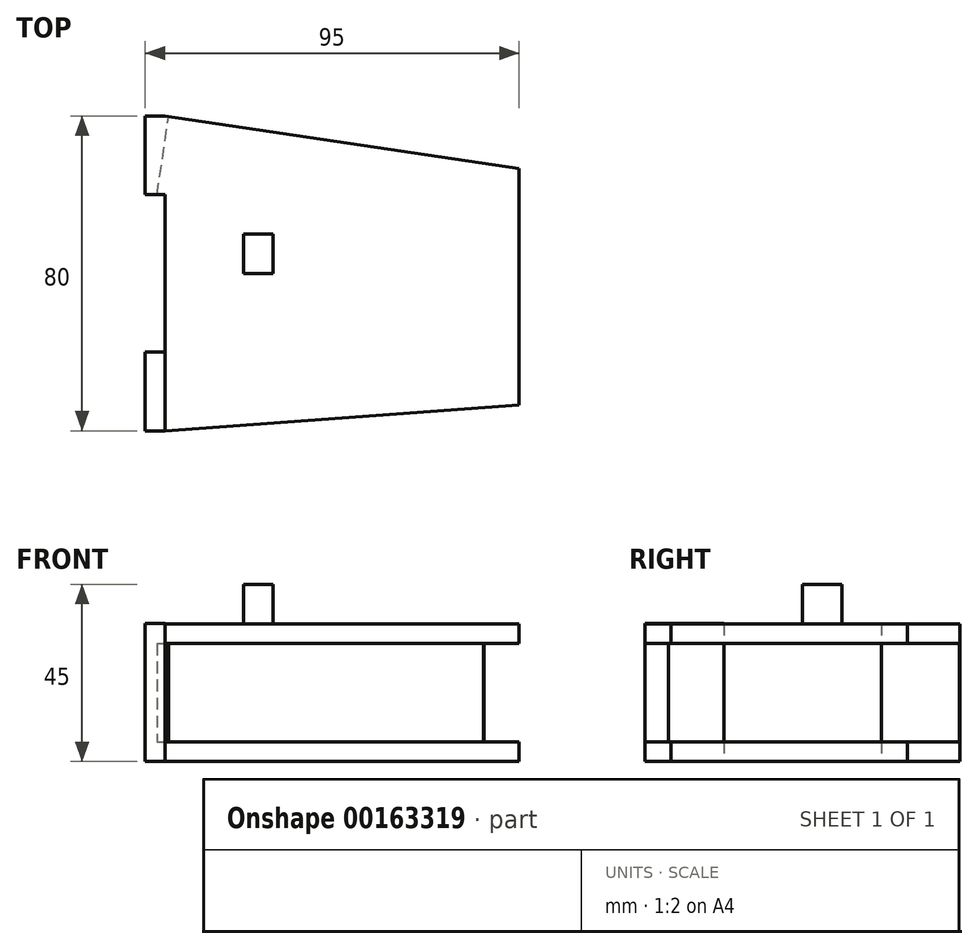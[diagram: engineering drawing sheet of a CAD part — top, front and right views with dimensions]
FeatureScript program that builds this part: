
annotation { "Feature Type Name" : "Feature", "Feature Type Description" : "" }
export const myFeature = defineFeature(function(context is Context, id is Id, definition is map)
    precondition{}
    {
        {
            var Q0;
            Q0=qCreatedBy(makeId("Top.planeOp"),FACE);
            var sketch = newSketch(context, id + "F0", { "sketchPlane" : qUnion([Q0])});
            skLineSegment(sketch, "E0", {"start": v(-88.53, 60) * mm, "end": v(-88.53, -20) * mm});
            skLineSegment(sketch, "E1", {"start": v(1.47, -13.38) * mm, "end": v(1.47, 46.62) * mm});
            skLineSegment(sketch, "E2", {"start": v(1.47, 46.62) * mm, "end": v(-88.53, 60) * mm});
            skLineSegment(sketch, "E3", {"start": v(-88.53, -20) * mm, "end": v(1.47, -13.38) * mm});
            skLineSegment(sketch, "E4", {"start": v(-88.53, 40) * mm, "end": v(-88.53, 0) * mm});
            skLineSegment(sketch, "E5.bottom", {"start": v(-88.53, 60) * mm, "end": v(-93.53, 60) * mm});
            skLineSegment(sketch, "E5.top", {"start": v(-88.53, 40) * mm, "end": v(-93.53, 40) * mm});
            skLineSegment(sketch, "E5.left", {"start": v(-88.53, 60) * mm, "end": v(-88.53, 40) * mm});
            skLineSegment(sketch, "E5.right", {"start": v(-93.53, 60) * mm, "end": v(-93.53, 40) * mm});
            skLineSegment(sketch, "E6.bottom", {"start": v(-88.53, 0) * mm, "end": v(-93.53, 0) * mm});
            skLineSegment(sketch, "E6.top", {"start": v(-88.53, -20) * mm, "end": v(-93.53, -20) * mm});
            skLineSegment(sketch, "E6.left", {"start": v(-88.53, 0) * mm, "end": v(-88.53, -20) * mm});
            skLineSegment(sketch, "E6.right", {"start": v(-93.53, 0) * mm, "end": v(-93.53, -20) * mm});
            skSolve(sketch);
        }
        {
            var Q0;
            Q0=makeQuery(id+"F0.imprint","IMPRINT",FACE,{"disambiguationData":[TD([[makeQuery(id+"F0.imprint","IMPRINT",EDGE,{"derivedFrom":sQuery(id+"F0.wireOp",EDGE,"E1")}),1.0]])]});
            var Q1;
            Q1=makeQuery(id+"F0.imprint","IMPRINT",FACE,{"disambiguationData":[TD([[makeQuery(id+"F0.imprint","IMPRINT",EDGE,{"derivedFrom":sQuery(id+"F0.wireOp",EDGE,"E5.bottom")}),1.0]])]});
            var Q2;
            Q2=makeQuery(id+"F0.imprint","IMPRINT",FACE,{"disambiguationData":[TD([[makeQuery(id+"F0.imprint","IMPRINT",EDGE,{"derivedFrom":sQuery(id+"F0.wireOp",EDGE,"E6.bottom")}),1.0]])]});
            extrude(context, id + "F1", {"entities" : qUnion([Q0, Q1, Q2]), "depth" : 35 * mm});
        }
        {
            var Q0;
            Q0=makeQuery(id+"F1.opExtrude","SWEPT_FACE",FACE,{"disambiguationData":[OSD([sQuery(id+"F0.wireOp",EDGE,"E2")])]});
            var sketch = newSketch(context, id + "F2", { "sketchPlane" : qUnion([Q0])});
            skLineSegment(sketch, "E7.bottom", {"start": v(5.4, 5) * mm, "end": v(95.4, 5) * mm});
            skLineSegment(sketch, "E7.top", {"start": v(5.4, 30) * mm, "end": v(95.4, 30) * mm});
            skLineSegment(sketch, "E7.left", {"start": v(5.4, 5) * mm, "end": v(5.4, 30) * mm});
            skLineSegment(sketch, "E7.right", {"start": v(95.4, 5) * mm, "end": v(95.4, 30) * mm});
            skSolve(sketch);
        }
        {
            var Q0;
            Q0=makeQuery(id+"F2.imprint","IMPRINT",FACE,{"disambiguationData":[TD([[makeQuery(id+"F2.imprint","IMPRINT",EDGE,{"derivedFrom":sQuery(id+"F2.wireOp",EDGE,"E7.bottom")}),1.0]])]});
            extrude(context, id + "F3", {"entities" : qUnion([Q0]), "operationType" : NewBodyOperationType.REMOVE, "endBound" : BoundingType.THROUGH_ALL, "oppositeDirection" : true, "depth" : 25 * mm});
        }
        {
            var Q0;
            {var subQ0=sQuery(id+"F0.wireOp",EDGE,"E6.right");Q0=makeQuery(id+"F3.boolean.opBoolean","SPLIT",FACE,{"disambiguationData":[TD([makeQuery(id+"F3.opExtrude","SWEPT_FACE",FACE,{"disambiguationData":[OSD([sQuery(id+"F2.wireOp",EDGE,"E7.bottom")])]})])],"derivedFrom":makeQuery(id+"F1.opExtrude","SWEPT_FACE",FACE,{"disambiguationData":[OSD([subQ0])]})});}
            var sketch = newSketch(context, id + "F4", { "sketchPlane" : qUnion([Q0])});
            skLineSegment(sketch, "E8.bottom", {"start": v(20, 0) * mm, "end": v(0, 0) * mm});
            skLineSegment(sketch, "E8.top", {"start": v(20, 35.14) * mm, "end": v(0, 35.14) * mm});
            skLineSegment(sketch, "E8.left", {"start": v(20, 0) * mm, "end": v(20, 35.14) * mm});
            skLineSegment(sketch, "E8.right", {"start": v(0, 0) * mm, "end": v(0, 35.14) * mm});
            skSolve(sketch);
        }
        {
            var Q0;
            Q0 = qSketchRegion(id + "F4", true);
            extrude(context, id + "F5", {"entities" : qUnion([Q0]), "operationType" : NewBodyOperationType.ADD, "oppositeDirection" : true, "depth" : 5 * mm});
        }
        {
            var Q0;
            Q0=makeQuery(id+"F1.opExtrude","SWEPT_FACE",FACE,{"disambiguationData":[OSD([sQuery(id+"F0.wireOp",EDGE,"E1")])]});
            var sketch = newSketch(context, id + "F6", { "sketchPlane" : qUnion([Q0])});
            skLineSegment(sketch, "E9.bottom", {"start": v(46.62, 30) * mm, "end": v(-13.38, 30) * mm});
            skLineSegment(sketch, "E9.top", {"start": v(46.62, 5) * mm, "end": v(-13.38, 5) * mm});
            skLineSegment(sketch, "E9.left", {"start": v(46.62, 30) * mm, "end": v(46.62, 5) * mm});
            skLineSegment(sketch, "E9.right", {"start": v(-13.38, 30) * mm, "end": v(-13.38, 5) * mm});
            skSolve(sketch);
        }
        {
            var Q0;
            Q0=makeQuery(id+"F6.imprint","IMPRINT",FACE,{"disambiguationData":[TD([[makeQuery(id+"F6.imprint","IMPRINT",EDGE,{"derivedFrom":sQuery(id+"F6.wireOp",EDGE,"E9.bottom")}),1.0]])]});
            extrude(context, id + "F7", {"entities" : qUnion([Q0]), "operationType" : NewBodyOperationType.REMOVE, "endBound" : BoundingType.UP_TO_NEXT, "oppositeDirection" : true, "depth" : 25 * mm});
        }
        {
            var Q0;
            Q0=makeQuery(id+"F7.boolean.opBoolean","COPY",FACE,{"derivedFrom":makeQuery(id+"F7.opExtrude","SWEPT_FACE",FACE,{"disambiguationData":[OSD([sQuery(id+"F6.wireOp",EDGE,"E9.right")])]})});
            var sketch = newSketch(context, id + "F8", { "sketchPlane" : qUnion([Q0])});
            skLineSegment(sketch, "E10.bottom", {"start": v(7.45, 30) * mm, "end": v(-1.47, 30) * mm});
            skLineSegment(sketch, "E10.top", {"start": v(7.45, 5) * mm, "end": v(-1.47, 5) * mm});
            skLineSegment(sketch, "E10.left", {"start": v(7.45, 30) * mm, "end": v(7.45, 5) * mm});
            skLineSegment(sketch, "E10.right", {"start": v(-1.47, 30) * mm, "end": v(-1.47, 5) * mm});
            skSolve(sketch);
        }
        {
            var Q0;
            Q0=makeQuery(id+"F8.imprint","IMPRINT",FACE,{"disambiguationData":[TD([[makeQuery(id+"F8.imprint","IMPRINT",EDGE,{"derivedFrom":sQuery(id+"F8.wireOp",EDGE,"E10.bottom")}),1.0]])]});
            extrude(context, id + "F9", {"entities" : qUnion([Q0]), "operationType" : NewBodyOperationType.REMOVE, "endBound" : BoundingType.SYMMETRIC, "oppositeDirection" : true, "depth" : 25 * mm});
        }
        {
            var Q0;
            Q0=makeQuery(id+"F9.boolean.opBoolean","COPY",FACE,{"derivedFrom":makeQuery(id+"F9.opExtrude","SWEPT_FACE",FACE,{"disambiguationData":[OSD([sQuery(id+"F8.wireOp",EDGE,"E10.left")])]})});
            var sketch = newSketch(context, id + "F10", { "sketchPlane" : qUnion([Q0])});
            skLineSegment(sketch, "E11.bottom", {"start": v(-14.03, 5) * mm, "end": v(-13.38, 5) * mm});
            skLineSegment(sketch, "E11.top", {"start": v(-14.03, 30) * mm, "end": v(-13.38, 30) * mm});
            skLineSegment(sketch, "E11.left", {"start": v(-14.03, 5) * mm, "end": v(-14.03, 30) * mm});
            skLineSegment(sketch, "E11.right", {"start": v(-13.38, 5) * mm, "end": v(-13.38, 30) * mm});
            skSolve(sketch);
        }
        {
            var Q0;
            Q0 = qSketchRegion(id + "F10", true);
            extrude(context, id + "F11", {"entities" : qUnion([Q0]), "operationType" : NewBodyOperationType.REMOVE, "endBound" : BoundingType.SYMMETRIC, "oppositeDirection" : true, "depth" : 10 * mm});
        }
        {
            var Q0;
            Q0=makeQuery(id+"F1.opExtrude","CAP_FACE",FACE,{"disambiguationData":[OSD([sQuery(id+"F0.wireOp",EDGE,"E1"),sQuery(id+"F0.wireOp",EDGE,"E2"),sQuery(id+"F0.wireOp",EDGE,"E3"),sQuery(id+"F0.wireOp",EDGE,"E4"),sQuery(id+"F0.wireOp",EDGE,"E5.bottom"),sQuery(id+"F0.wireOp",EDGE,"E5.top"),sQuery(id+"F0.wireOp",EDGE,"E5.right"),sQuery(id+"F0.wireOp",EDGE,"E6.bottom"),sQuery(id+"F0.wireOp",EDGE,"E6.top"),sQuery(id+"F0.wireOp",EDGE,"E6.right")])],"isStart":false});
            var sketch = newSketch(context, id + "F12", { "sketchPlane" : qUnion([Q0])});
            skLineSegment(sketch, "E12.bottom", {"start": v(-68.53, 30) * mm, "end": v(-61.03, 30) * mm});
            skLineSegment(sketch, "E12.top", {"start": v(-68.53, 20) * mm, "end": v(-61.03, 20) * mm});
            skLineSegment(sketch, "E12.left", {"start": v(-68.53, 30) * mm, "end": v(-68.53, 20) * mm});
            skLineSegment(sketch, "E12.right", {"start": v(-61.03, 30) * mm, "end": v(-61.03, 20) * mm});
            skSolve(sketch);
        }
        {
            var Q0;
            Q0=makeQuery(id+"F12.imprint","IMPRINT",FACE,{"disambiguationData":[TD([[makeQuery(id+"F12.imprint","IMPRINT",EDGE,{"derivedFrom":sQuery(id+"F12.wireOp",EDGE,"E12.bottom")}),-1.0]])]});
            extrude(context, id + "F13", {"entities" : qUnion([Q0]), "operationType" : NewBodyOperationType.ADD, "depth" : 10 * mm});
        }
    });
